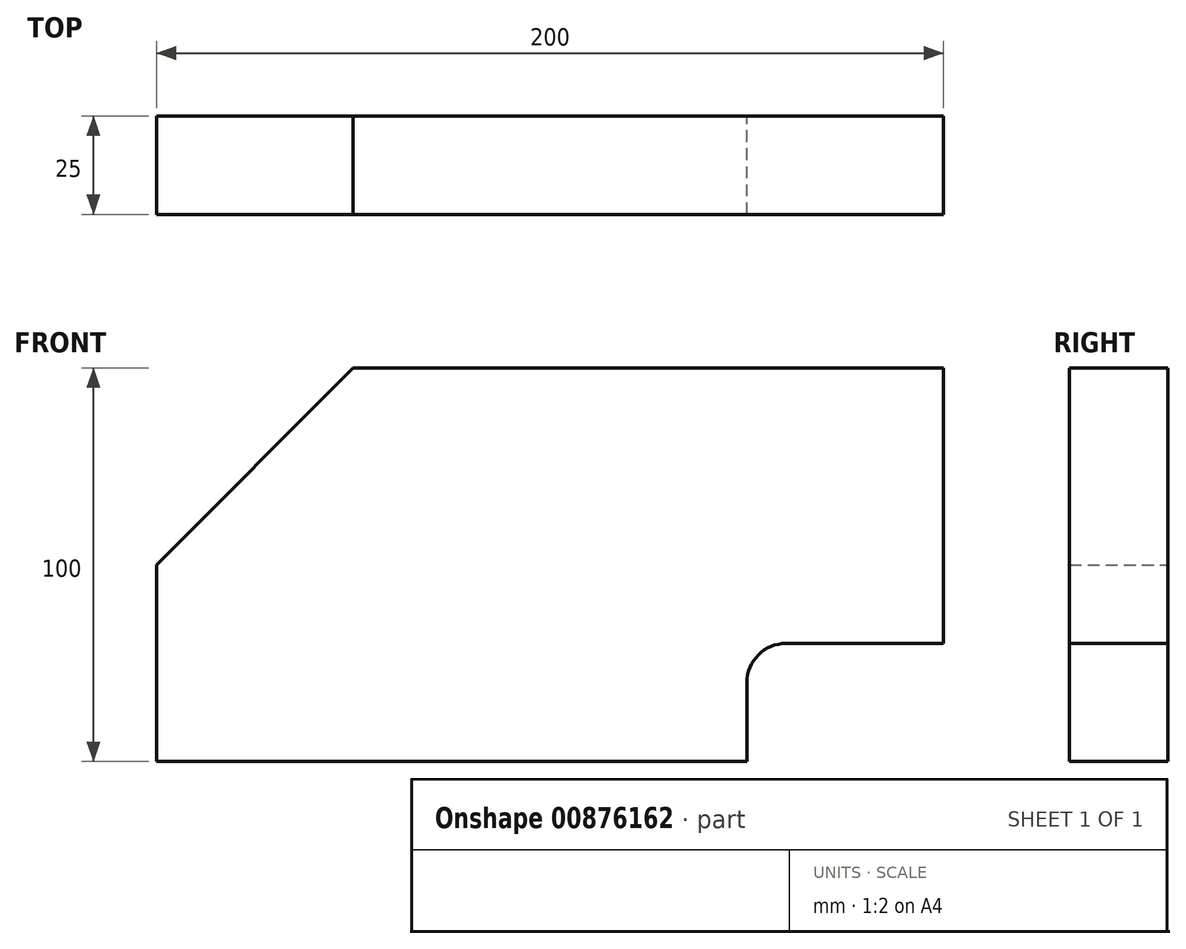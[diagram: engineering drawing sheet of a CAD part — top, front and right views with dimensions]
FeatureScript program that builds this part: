
annotation { "Feature Type Name" : "Feature", "Feature Type Description" : "" }
export const myFeature = defineFeature(function(context is Context, id is Id, definition is map)
    precondition{}
    {
        {
            var Q0;
            Q0=qCreatedBy(makeId("Front.planeOp"),FACE);
            var sketch = newSketch(context, id + "F0", { "sketchPlane" : qUnion([Q0])});
            skLineSegment(sketch, "E0", {"start": v(-150, 0) * mm, "end": v(-150, 50) * mm});
            skLineSegment(sketch, "E1", {"start": v(-150, 50) * mm, "end": v(-100, 100) * mm});
            skLineSegment(sketch, "E2", {"start": v(-100, 100) * mm, "end": v(50, 100) * mm});
            skLineSegment(sketch, "E3", {"start": v(50, 100) * mm, "end": v(50, 30) * mm});
            skLineSegment(sketch, "E4", {"start": v(50, 30) * mm, "end": v(10, 30) * mm});
            skLineSegment(sketch, "E5", {"start": v(0, 20) * mm, "end": v(0, 0) * mm});
            skLineSegment(sketch, "E6", {"start": v(0, 0) * mm, "end": v(-150, 0) * mm});
            skPoint(sketch, "E7.visualSharp", {"position": v(0, 30) * mm});
            skArc(sketch, "E7.filletArc", {"start": v(10, 30) * mm, "mid": v(2.93, 27.07) * mm, "end": v(0, 20) * mm});
            skSolve(sketch);
        }
        {
            var Q0;
            Q0 = qSketchRegion(id + "F0", true);
            extrude(context, id + "F1", {"entities" : qUnion([Q0]), "depth" : 25 * mm, "offsetDistance" : 25 * mm});
        }
        {
            var Q0;
            Q0=makeQuery(id+"F0.imprint","IMPRINT",FACE,{"disambiguationData":[TD([[makeQuery(id+"F0.imprint","IMPRINT",EDGE,{"derivedFrom":sQuery(id+"F0.wireOp",EDGE,"E0")}),-1.0]])]});
            extrude(context, id + "F2", {"entities" : qUnion([Q0]), "operationType" : NewBodyOperationType.ADD, "depth" : 25 * mm, "offsetDistance" : 25 * mm});
        }
    });
